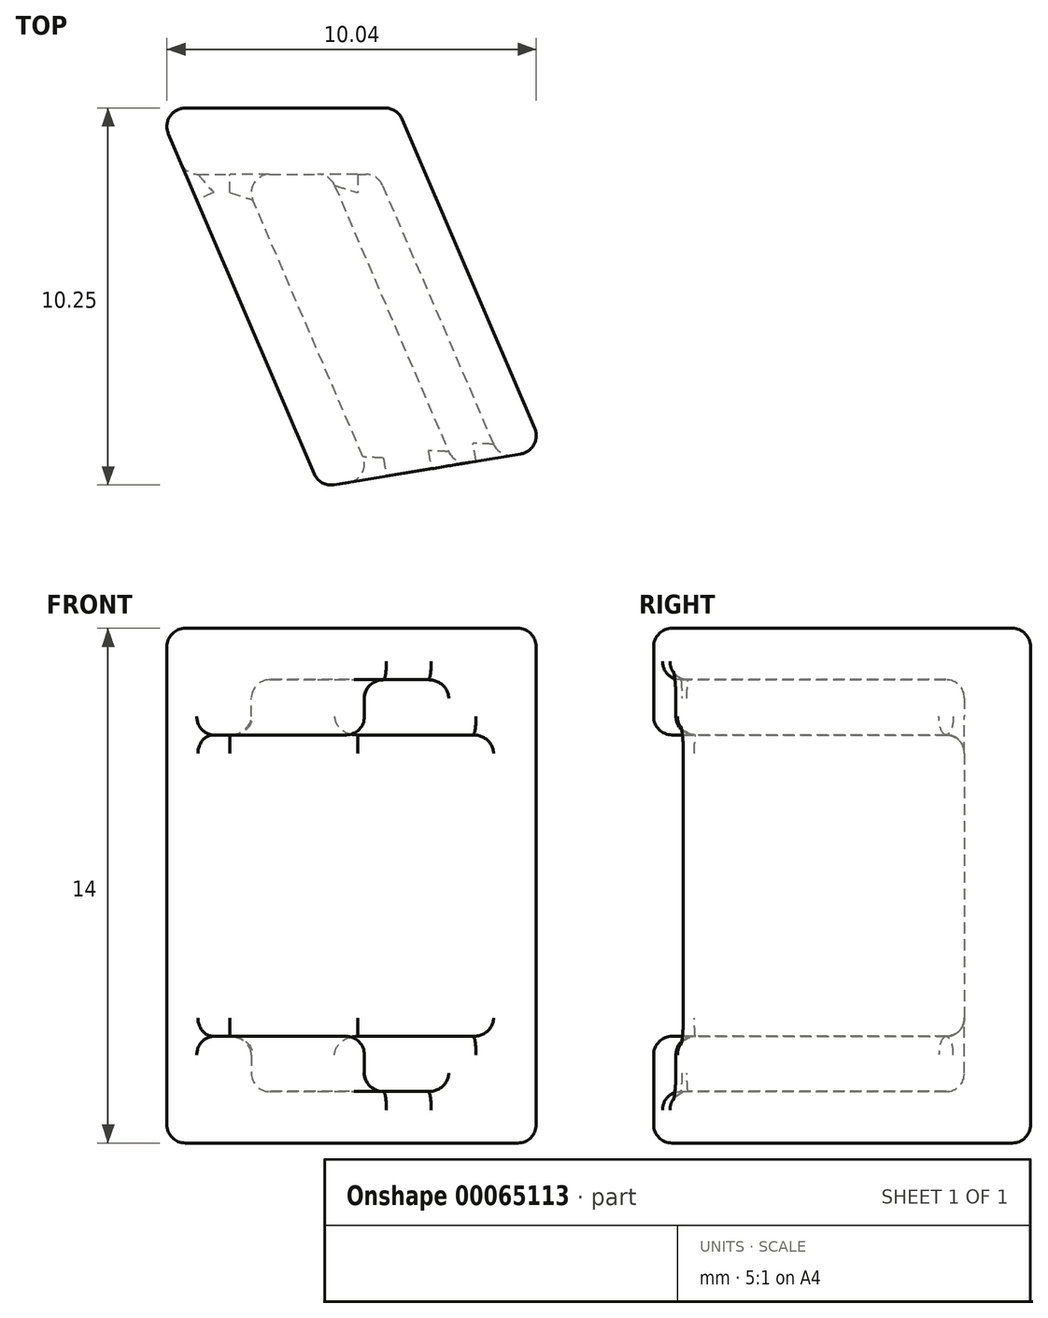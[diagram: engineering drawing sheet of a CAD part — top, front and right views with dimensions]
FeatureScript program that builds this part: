
annotation { "Feature Type Name" : "Feature", "Feature Type Description" : "" }
export const myFeature = defineFeature(function(context is Context, id is Id, definition is map)
    precondition{}
    {
        {
            var Q0;
            Q0=qCreatedBy(makeId("Top.planeOp"),FACE);
            var sketch = newSketch(context, id + "F0", { "sketchPlane" : qUnion([Q0])});
            skLineSegment(sketch, "E0", {"start": v(22.5, 2.5) * mm, "end": v(23.5, 15.5) * mm, "construction": true});
            skLineSegment(sketch, "E1", {"start": v(23.5, 15.5) * mm, "end": v(23.42, 15.69) * mm, "construction": true});
            skLineSegment(sketch, "E2", {"start": v(19, 26) * mm, "end": v(25.53, 26) * mm});
            skLineSegment(sketch, "E3", {"start": v(25.53, 26) * mm, "end": v(29.51, 16.7) * mm});
            skLineSegment(sketch, "E4", {"start": v(29.6, 16.5) * mm, "end": v(27.86, -6) * mm, "construction": true});
            skLineSegment(sketch, "E5", {"start": v(27.86, -6) * mm, "end": v(-27, -6) * mm, "construction": true});
            skLineSegment(sketch, "E6", {"start": v(-27, -6) * mm, "end": v(-36.5, 29.01) * mm, "construction": true});
            skLineSegment(sketch, "E7", {"start": v(-36.5, 29.01) * mm, "end": v(-36.5, 32) * mm, "construction": true});
            skLineSegment(sketch, "E8", {"start": v(-36.5, 32) * mm, "end": v(-18.5, 32) * mm, "construction": true});
            skLineSegment(sketch, "E9", {"start": v(-18.5, 32) * mm, "end": v(-18.5, 26) * mm, "construction": true});
            skLineSegment(sketch, "E10", {"start": v(-18.5, 26) * mm, "end": v(-23.5, 26) * mm, "construction": true});
            skLineSegment(sketch, "E11", {"start": v(-23.5, 26) * mm, "end": v(-26.7, 15.8) * mm, "construction": true});
            skLineSegment(sketch, "E12", {"start": v(-26.7, 15.8) * mm, "end": v(-23.5, 4) * mm, "construction": true});
            skLineSegment(sketch, "E13", {"start": v(-23.5, 4) * mm, "end": v(-19.5, 0) * mm, "construction": true});
            skLineSegment(sketch, "E14", {"start": v(-19.5, 0) * mm, "end": v(19.5, 0) * mm, "construction": true});
            skLineSegment(sketch, "E15", {"start": v(19.5, 0) * mm, "end": v(22.5, 2.5) * mm, "construction": true});
            skLineSegment(sketch, "E16", {"start": v(23.5, 15.5) * mm, "end": v(29.6, 16.5) * mm, "construction": true});
            skLineSegment(sketch, "E17", {"start": v(23.42, 15.69) * mm, "end": v(29.51, 16.7) * mm});
            skLineSegment(sketch, "E18", {"start": v(23.42, 15.69) * mm, "end": v(19, 26) * mm});
            skLineSegment(sketch, "E19", {"start": v(29.51, 16.7) * mm, "end": v(29.6, 16.5) * mm, "construction": true});
            skSolve(sketch);
        }
        {
            var Q0;
            Q0=qCreatedBy(makeId("Top.planeOp"),FACE);
            var sketch = newSketch(context, id + "F1", { "sketchPlane" : qUnion([Q0])});
            skLineSegment(sketch, "E20.0", {"start": v(23.42, 15.69) * mm, "end": v(19.77, 24.2) * mm, "construction": true});
            skLineSegment(sketch, "E21.0", {"start": v(19, 26) * mm, "end": v(25.53, 26) * mm, "construction": true});
            skLineSegment(sketch, "E22.0", {"start": v(25.53, 26) * mm, "end": v(29.51, 16.7) * mm, "construction": true});
            skLineSegment(sketch, "E23", {"start": v(19.77, 24.2) * mm, "end": v(25, 24.2) * mm});
            skLineSegment(sketch, "E24", {"start": v(25, 24.2) * mm, "end": v(28.31, 16.46) * mm});
            skLineSegment(sketch, "E25", {"start": v(28.31, 16.46) * mm, "end": v(29.51, 16.7) * mm, "construction": true});
            skPoint(sketch, "E26.orphan", {"position": v(23.5, 15.5) * mm});
            skLineSegment(sketch, "E27.0", {"start": v(-27, -6) * mm, "end": v(-28.63, 0) * mm});
            skLineSegment(sketch, "E28.0", {"start": v(-15, -6) * mm, "end": v(-27, -6) * mm});
            skLineSegment(sketch, "E29", {"start": v(-28.63, 0) * mm, "end": v(-26.56, 0) * mm});
            skLineSegment(sketch, "E30", {"start": v(-26.56, 0) * mm, "end": v(-25.31, -4.6) * mm});
            skLineSegment(sketch, "E31", {"start": v(-25.31, -4.6) * mm, "end": v(-15, -4.6) * mm});
            skLineSegment(sketch, "E32", {"start": v(-15, -4.6) * mm, "end": v(-15, -6) * mm});
            skLineSegment(sketch, "E33", {"start": v(19.77, 24.2) * mm, "end": v(23.5, 15.5) * mm});
            skLineSegment(sketch, "E34", {"start": v(23.5, 15.5) * mm, "end": v(28.31, 16.46) * mm});
            skSolve(sketch);
        }
        {
            var Q0;
            Q0=qCreatedBy(makeId("Top.planeOp"),FACE);
            var sketch = newSketch(context, id + "F2", { "sketchPlane" : qUnion([Q0])});
            skLineSegment(sketch, "E35", {"start": v(22.72, 20.88) * mm, "end": v(24.74, 21.75) * mm, "construction": true});
            skLineSegment(sketch, "E36", {"start": v(24.74, 21.75) * mm, "end": v(26.79, 16.97) * mm});
            skLineSegment(sketch, "E37", {"start": v(26.79, 16.97) * mm, "end": v(24.77, 16.1) * mm, "construction": true});
            skLineSegment(sketch, "E38", {"start": v(24.77, 16.1) * mm, "end": v(22.72, 20.88) * mm});
            skLineSegment(sketch, "E39", {"start": v(-23.4, -1.4) * mm, "end": v(-18.2, -1.4) * mm});
            skLineSegment(sketch, "E40", {"start": v(-18.2, -1.4) * mm, "end": v(-18.2, -3.6) * mm});
            skLineSegment(sketch, "E41", {"start": v(-18.2, -3.6) * mm, "end": v(-23.4, -3.6) * mm});
            skLineSegment(sketch, "E42", {"start": v(-23.4, -3.6) * mm, "end": v(-23.4, -1.4) * mm});
            skLineSegment(sketch, "E43", {"start": v(-33.35, 26.55) * mm, "end": v(-31.22, 27.13) * mm});
            skLineSegment(sketch, "E44", {"start": v(-31.22, 27.13) * mm, "end": v(-29.86, 22.11) * mm});
            skLineSegment(sketch, "E45", {"start": v(-29.86, 22.11) * mm, "end": v(-31.99, 21.53) * mm});
            skLineSegment(sketch, "E46", {"start": v(-31.99, 21.53) * mm, "end": v(-33.35, 26.55) * mm});
            skLineSegment(sketch, "E47", {"start": v(-32.28, 26.84) * mm, "end": v(-30.92, 21.82) * mm, "construction": true});
            skLineSegment(sketch, "E48", {"start": v(-23.4, -2.5) * mm, "end": v(-18.2, -2.5) * mm, "construction": true});
            skLineSegment(sketch, "E49", {"start": v(25.78, 16.53) * mm, "end": v(23.73, 21.31) * mm, "construction": true});
            skLineSegment(sketch, "E50", {"start": v(-23.4, -3.6) * mm, "end": v(-27, -6) * mm, "construction": true});
            skLineSegment(sketch, "E51", {"start": v(-33.35, 26.55) * mm, "end": v(-36.5, 29.01) * mm, "construction": true});
            skLineSegment(sketch, "E52", {"start": v(24.74, 21.75) * mm, "end": v(25.53, 26) * mm, "construction": true});
            skLineSegment(sketch, "E53", {"start": v(26.79, 16.97) * mm, "end": v(27.16, 16.1) * mm});
            skLineSegment(sketch, "E54", {"start": v(27.16, 16.1) * mm, "end": v(24.92, 15.74) * mm});
            skLineSegment(sketch, "E55", {"start": v(24.92, 15.74) * mm, "end": v(24.77, 16.1) * mm});
            skLineSegment(sketch, "E56", {"start": v(22.72, 20.88) * mm, "end": v(21.3, 24.2) * mm});
            skLineSegment(sketch, "E57", {"start": v(21.3, 24.2) * mm, "end": v(23.69, 24.2) * mm});
            skLineSegment(sketch, "E58", {"start": v(23.69, 24.2) * mm, "end": v(24.74, 21.75) * mm});
            skSolve(sketch);
        }
        {
            var Q0;
            Q0 = qSketchRegion(id + "F0", true);
            extrude(context, id + "F3", {"entities" : qUnion([Q0]), "depth" : 7 * mm});
        }
        {
            var Q0;
            Q0 = qSketchRegion(id + "F2", true);
            extrude(context, id + "F4", {"entities" : qUnion([Q0]), "operationType" : NewBodyOperationType.REMOVE, "depth" : 5.6 * mm});
        }
        {
            var Q0;
            Q0 = qSketchRegion(id + "F1", true);
            extrude(context, id + "F5", {"entities" : qUnion([Q0]), "operationType" : NewBodyOperationType.REMOVE, "depth" : 4.1 * mm});
        }
        {
            var Q0;
            Q0=makeQuery(id+"F4.boolean.opBoolean","COPY",EDGE,{"derivedFrom":makeQuery(id+"F4.opExtrude","CAP_EDGE",EDGE,{"disambiguationData":[OSD([sQuery(id+"F2.wireOp",EDGE,"E36"),sQuery(id+"F2.wireOp",EDGE,"E53"),sQuery(id+"F2.wireOp",EDGE,"E58")])],"isStart":false})});
            var Q1;
            Q1=makeQuery(id+"F5.boolean.opBoolean","INTERSECT",EDGE,{"derivedFrom":[makeQuery(id+"F4.boolean.opBoolean","COPY",FACE,{"derivedFrom":makeQuery(id+"F4.opExtrude","SWEPT_FACE",FACE,{"disambiguationData":[OSD([sQuery(id+"F2.wireOp",EDGE,"E36"),sQuery(id+"F2.wireOp",EDGE,"E53"),sQuery(id+"F2.wireOp",EDGE,"E58")])]})}),makeQuery(id+"F5.opExtrude","CAP_FACE",FACE,{"disambiguationData":[OSD([sQuery(id+"F1.wireOp",EDGE,"E23"),sQuery(id+"F1.wireOp",EDGE,"E24"),sQuery(id+"F1.wireOp",EDGE,"E33"),sQuery(id+"F1.wireOp",EDGE,"E34")])],"isStart":false})]});
            var Q2;
            Q2=makeQuery(id+"F5.boolean.opBoolean","INTERSECT",EDGE,{"derivedFrom":[makeQuery(id+"F4.boolean.opBoolean","COPY",FACE,{"derivedFrom":makeQuery(id+"F4.opExtrude","SWEPT_FACE",FACE,{"disambiguationData":[OSD([sQuery(id+"F2.wireOp",EDGE,"E38"),sQuery(id+"F2.wireOp",EDGE,"E55"),sQuery(id+"F2.wireOp",EDGE,"E56")])]})}),makeQuery(id+"F5.opExtrude","CAP_FACE",FACE,{"disambiguationData":[OSD([sQuery(id+"F1.wireOp",EDGE,"E23"),sQuery(id+"F1.wireOp",EDGE,"E24"),sQuery(id+"F1.wireOp",EDGE,"E33"),sQuery(id+"F1.wireOp",EDGE,"E34")])],"isStart":false})]});
            var Q3;
            Q3=makeQuery(id+"F4.boolean.opBoolean","COPY",EDGE,{"derivedFrom":makeQuery(id+"F4.opExtrude","CAP_EDGE",EDGE,{"disambiguationData":[OSD([sQuery(id+"F2.wireOp",EDGE,"E38"),sQuery(id+"F2.wireOp",EDGE,"E55"),sQuery(id+"F2.wireOp",EDGE,"E56")])],"isStart":false})});
            var Q4;
            Q4=makeQuery(id+"F4.boolean.opBoolean","COPY",EDGE,{"derivedFrom":makeQuery(id+"F4.opExtrude","CAP_EDGE",EDGE,{"disambiguationData":[OSD([sQuery(id+"F2.wireOp",EDGE,"E57")])],"isStart":false})});
            var Q5;
            Q5=makeQuery(id+"F4.boolean.opBoolean","COPY",EDGE,{"derivedFrom":makeQuery(id+"F4.opExtrude","SWEPT_EDGE",EDGE,{"disambiguationData":[OSD([sQuery(id+"F2.wireOp",EDGE,"E56"),sQuery(id+"F2.wireOp",EDGE,"E57")])]})});
            var Q6;
            Q6=makeQuery(id+"F4.boolean.opBoolean","COPY",EDGE,{"derivedFrom":makeQuery(id+"F4.opExtrude","SWEPT_EDGE",EDGE,{"disambiguationData":[OSD([sQuery(id+"F2.wireOp",EDGE,"E57"),sQuery(id+"F2.wireOp",EDGE,"E58")])]})});
            var Q7;
            Q7=makeQuery(id+"F5.boolean.opBoolean","COPY",EDGE,{"disambiguationData":[OD(0.0)],"derivedFrom":makeQuery(id+"F5.opExtrude","CAP_EDGE",EDGE,{"disambiguationData":[OSD([sQuery(id+"F1.wireOp",EDGE,"E23")])],"isStart":false})});
            var Q8;
            Q8=makeQuery(id+"F5.boolean.opBoolean","COPY",EDGE,{"disambiguationData":[OD(1.0)],"derivedFrom":makeQuery(id+"F5.opExtrude","CAP_EDGE",EDGE,{"disambiguationData":[OSD([sQuery(id+"F1.wireOp",EDGE,"E23")])],"isStart":false})});
            var Q9;
            Q9=makeQuery(id+"F5.boolean.opBoolean","COPY",EDGE,{"derivedFrom":makeQuery(id+"F5.opExtrude","SWEPT_EDGE",EDGE,{"disambiguationData":[OSD([sQuery(id+"F1.wireOp",EDGE,"E23"),sQuery(id+"F1.wireOp",EDGE,"E24")])]})});
            var Q10;
            Q10=makeQuery(id+"F5.boolean.opBoolean","COPY",EDGE,{"derivedFrom":makeQuery(id+"F5.opExtrude","CAP_EDGE",EDGE,{"disambiguationData":[OSD([sQuery(id+"F1.wireOp",EDGE,"E24")])],"isStart":false})});
            fillet(context, id + "F6", {"entities" : qUnion([Q0, Q1, Q2, Q3, Q4, Q5, Q6, Q7, Q8, Q9, Q10]), "radius" : .5 * mm, "tangentPropagation" : true, "allowEdgeOverflow" : false});
        }
        {
            var Q0;
            Q0=makeQuery(id+"F3.opExtrude","SWEPT_BODY",BODY,{"disambiguationData":[OSD([sQuery(id+"F0.wireOp",EDGE,"E1"),sQuery(id+"F0.wireOp",EDGE,"E2"),sQuery(id+"F0.wireOp",EDGE,"E3"),sQuery(id+"F0.wireOp",EDGE,"E16")])]});
            var Q1;
            Q1=qCreatedBy(makeId("Top.planeOp"),FACE);
            mirror(context, id + "F7", {"operationType" : NewBodyOperationType.ADD, "entities" : qUnion([Q0]), "mirrorPlane" : qUnion([Q1])});
        }
        {
            var Q0;
            {var subQ0=makeQuery(id+"F3.opExtrude","SWEPT_FACE",FACE,{"disambiguationData":[OSD([sQuery(id+"F0.wireOp",EDGE,"E1")])]});Q0=makeQuery(id+"F7.boolean.opBoolean","MERGE",FACE,{"derivedFrom":[subQ0,makeQuery(id+"F7.opPattern","COPY",FACE,{"derivedFrom":subQ0,"instanceName":"1"})]});}
            var Q1;
            {var subQ0=makeQuery(id+"F3.opExtrude","SWEPT_FACE",FACE,{"disambiguationData":[OSD([sQuery(id+"F0.wireOp",EDGE,"E16")])]});Q1=makeQuery(id+"F7.boolean.opBoolean","MERGE",FACE,{"derivedFrom":[subQ0,makeQuery(id+"F7.opPattern","COPY",FACE,{"derivedFrom":subQ0,"instanceName":"1"})]});}
            var Q2;
            {var subQ0=makeQuery(id+"F3.opExtrude","SWEPT_FACE",FACE,{"disambiguationData":[OSD([sQuery(id+"F0.wireOp",EDGE,"E2")])]});Q2=makeQuery(id+"F7.boolean.opBoolean","MERGE",FACE,{"derivedFrom":[subQ0,makeQuery(id+"F7.opPattern","COPY",FACE,{"derivedFrom":subQ0,"instanceName":"1"})]});}
            var Q3;
            {var subQ0=makeQuery(id+"F3.opExtrude","SWEPT_FACE",FACE,{"disambiguationData":[OSD([sQuery(id+"F0.wireOp",EDGE,"E3")])]});Q3=makeQuery(id+"F7.boolean.opBoolean","MERGE",FACE,{"derivedFrom":[subQ0,makeQuery(id+"F7.opPattern","COPY",FACE,{"derivedFrom":subQ0,"instanceName":"1"})]});}
            var Q4;
            {var subQ0=makeQuery(id+"F3.opExtrude","SWEPT_FACE",FACE,{"disambiguationData":[OSD([sQuery(id+"F0.wireOp",EDGE,"E17")])]});Q4=makeQuery(id+"F7.boolean.opBoolean","MERGE",FACE,{"derivedFrom":[subQ0,makeQuery(id+"F7.opPattern","COPY",FACE,{"derivedFrom":subQ0,"instanceName":"1"})]});}
            var Q5;
            {var subQ0=makeQuery(id+"F3.opExtrude","SWEPT_FACE",FACE,{"disambiguationData":[OSD([sQuery(id+"F0.wireOp",EDGE,"E18")])]});Q5=makeQuery(id+"F7.boolean.opBoolean","MERGE",FACE,{"derivedFrom":[subQ0,makeQuery(id+"F7.opPattern","COPY",FACE,{"derivedFrom":subQ0,"instanceName":"1"})]});}
            fillet(context, id + "F8", {"entities" : qUnion([Q0, Q1, Q2, Q3, Q4, Q5]), "radius" : 0.5 * mm, "tangentPropagation" : true, "allowEdgeOverflow" : false});
        }
    });
